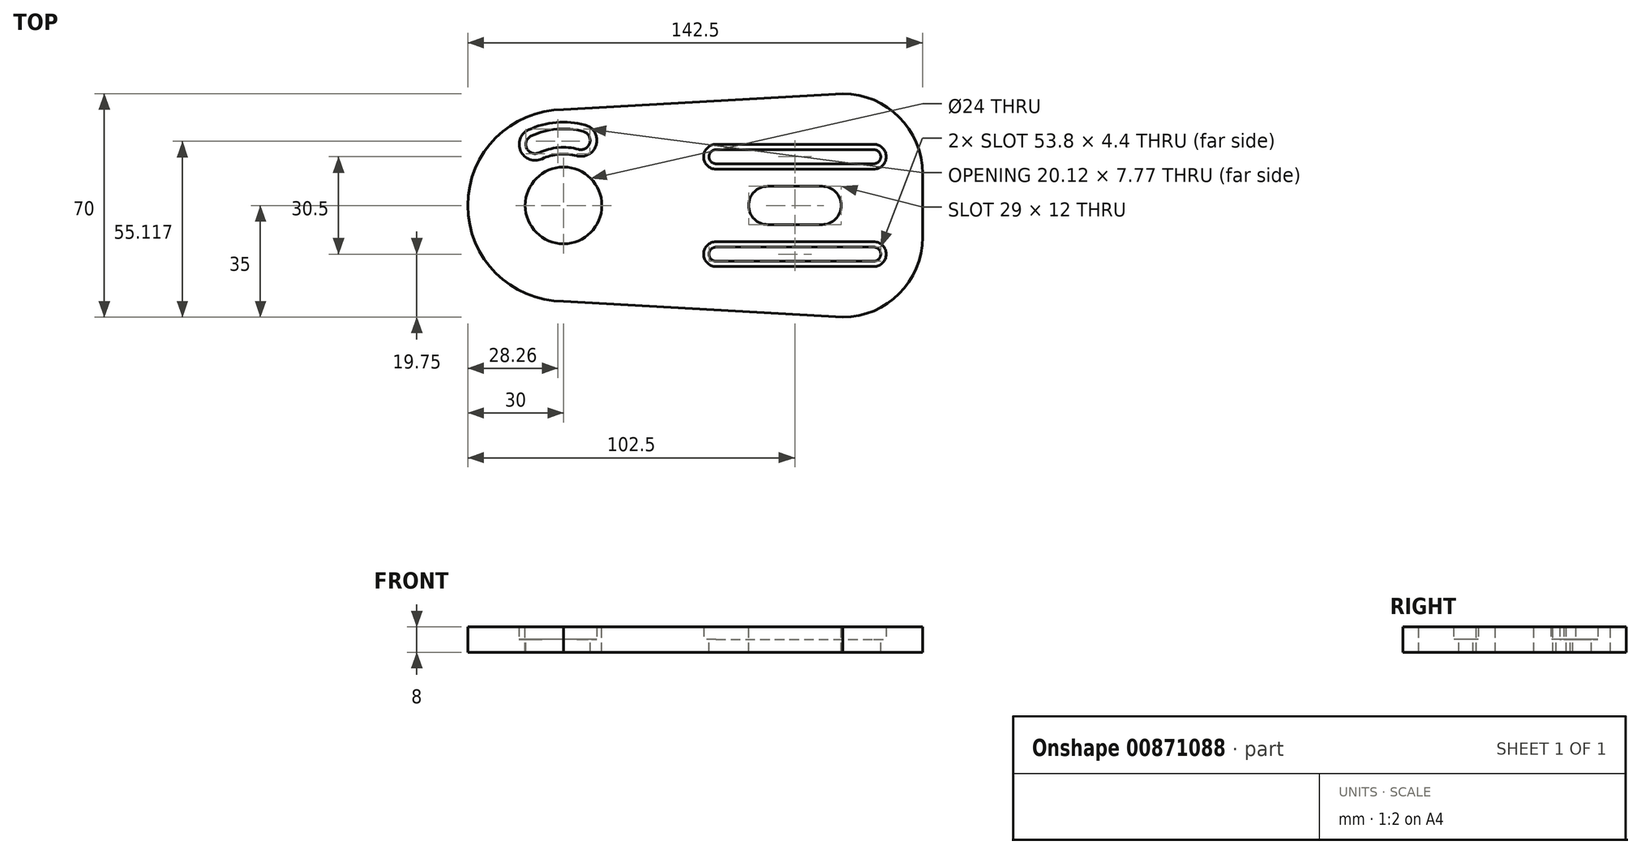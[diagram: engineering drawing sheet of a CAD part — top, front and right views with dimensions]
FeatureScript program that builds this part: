
annotation { "Feature Type Name" : "Feature", "Feature Type Description" : "" }
export const myFeature = defineFeature(function(context is Context, id is Id, definition is map)
    precondition{}
    {
        {
            var Q0;
            Q0=qCreatedBy(makeId("Top.planeOp"),FACE);
            var sketch = newSketch(context, id + "F0", { "sketchPlane" : qUnion([Q0])});
            skLineSegment(sketch, "E0.bottom", {"start": v(39.15, 35) * mm, "end": v(-48.35, 35) * mm, "construction": true});
            skLineSegment(sketch, "E0.top", {"start": v(39.15, -35) * mm, "end": v(-48.35, -35) * mm, "construction": true});
            skLineSegment(sketch, "E0.left", {"start": v(64.15, 10) * mm, "end": v(64.15, -10) * mm});
            skPoint(sketch, "E0.middle", {"position": v(0, 0) * mm});
            skCircle(sketch, "E1", {"center": v(-48.35, 0) * mm, "radius": 12 * mm});
            skArc(sketch, "E2.filletArc", {"start": v(64.15, 10) * mm, "mid": v(56.83, 27.68) * mm, "end": v(39.15, 35) * mm});
            skArc(sketch, "E3.filletArc", {"start": v(39.15, -35) * mm, "mid": v(56.83, -27.68) * mm, "end": v(64.15, -10) * mm});
            skLineSegment(sketch, "E4.bottom", {"start": v(32.65, 6) * mm, "end": v(24.15, 6) * mm});
            skPoint(sketch, "E4.middle", {"position": v(24.15, 0) * mm});
            skLineSegment(sketch, "E5", {"start": v(-48.35, 0) * mm, "end": v(-49.94, 18.13) * mm, "construction": true});
            skPoint(sketch, "E6", {"position": v(64.15, 0) * mm});
            skArc(sketch, "E7", {"start": v(-59.36, 23.66) * mm, "mid": v(-61.78, 17.02) * mm, "end": v(-55.14, 14.6) * mm});
            skArc(sketch, "E8", {"start": v(-58.47, 21.76) * mm, "mid": v(-59.88, 17.9) * mm, "end": v(-56.03, 16.5) * mm});
            skArc(sketch, "E9", {"start": v(-43.65, 17.58) * mm, "mid": v(-40.1, 19.64) * mm, "end": v(-42.16, 23.19) * mm});
            skArc(sketch, "E10.trimOffspring", {"start": v(-44.2, 15.55) * mm, "mid": v(-49.75, 16.04) * mm, "end": v(-55.14, 14.6) * mm});
            skArc(sketch, "E11.trimOffspring", {"start": v(-43.65, 17.58) * mm, "mid": v(-49.94, 18.13) * mm, "end": v(-56.03, 16.5) * mm});
            skArc(sketch, "E12.trimOffspring", {"start": v(-42.16, 23.19) * mm, "mid": v(-50.44, 23.9) * mm, "end": v(-58.47, 21.76) * mm});
            skArc(sketch, "E13.trimOffspring", {"start": v(-41.62, 25.22) * mm, "mid": v(-50.62, 26) * mm, "end": v(-59.36, 23.66) * mm});
            skArc(sketch, "E14.trimOffspring", {"start": v(-44.2, 15.55) * mm, "mid": v(-38.08, 19.1) * mm, "end": v(-41.62, 25.22) * mm});
            skCircle(sketch, "E15", {"center": v(-48.35, 0) * mm, "radius": 21.1 * mm, "construction": true});
            skLineSegment(sketch, "E16", {"start": v(32.65, 0) * mm, "end": v(24.15, 0) * mm, "construction": true});
            skArc(sketch, "E17", {"start": v(32.65, -6) * mm, "mid": v(38.65, 0) * mm, "end": v(32.65, 6) * mm});
            skLineSegment(sketch, "E18", {"start": v(24.15, 0) * mm, "end": v(24.15, 6) * mm, "construction": true});
            skLineSegment(sketch, "E19.MirrorCS", {"start": v(32.65, -6) * mm, "end": v(24.15, -6) * mm});
            skLineSegment(sketch, "E20.MirrorCS", {"start": v(15.65, 6) * mm, "end": v(24.15, 6) * mm});
            skArc(sketch, "E21.MirrorCS", {"start": v(15.65, -6) * mm, "mid": v(9.65, 0) * mm, "end": v(15.65, 6) * mm});
            skLineSegment(sketch, "E22.MirrorCS", {"start": v(15.65, -6) * mm, "end": v(24.15, -6) * mm});
            skArc(sketch, "E23", {"start": v(-0.55, -11.35) * mm, "mid": v(-4.45, -15.25) * mm, "end": v(-0.55, -19.15) * mm});
            skArc(sketch, "E24", {"start": v(-0.55, -13.05) * mm, "mid": v(-2.75, -15.25) * mm, "end": v(-0.55, -17.45) * mm});
            skLineSegment(sketch, "E25", {"start": v(-0.55, -11.35) * mm, "end": v(24.15, -11.35) * mm});
            skLineSegment(sketch, "E26", {"start": v(-0.55, -15.25) * mm, "end": v(24.15, -15.25) * mm, "construction": true});
            skLineSegment(sketch, "E27", {"start": v(-0.55, -13.05) * mm, "end": v(24.15, -13.05) * mm});
            skLineSegment(sketch, "E28.MirrorCS", {"start": v(-0.55, -17.45) * mm, "end": v(24.15, -17.45) * mm});
            skLineSegment(sketch, "E29.MirrorCS", {"start": v(-0.55, -19.15) * mm, "end": v(24.15, -19.15) * mm});
            skLineSegment(sketch, "E30.MirrorCS", {"start": v(48.85, -11.35) * mm, "end": v(24.15, -11.35) * mm});
            skLineSegment(sketch, "E31.MirrorCS", {"start": v(48.85, -13.05) * mm, "end": v(24.15, -13.05) * mm});
            skLineSegment(sketch, "E32.MirrorCS", {"start": v(48.85, -17.45) * mm, "end": v(24.15, -17.45) * mm});
            skLineSegment(sketch, "E33.MirrorCS", {"start": v(48.85, -19.15) * mm, "end": v(24.15, -19.15) * mm});
            skArc(sketch, "E34.MirrorCS", {"start": v(48.85, -13.05) * mm, "mid": v(51.05, -15.25) * mm, "end": v(48.85, -17.45) * mm});
            skArc(sketch, "E35.MirrorCS", {"start": v(48.85, -11.35) * mm, "mid": v(52.75, -15.25) * mm, "end": v(48.85, -19.15) * mm});
            skLineSegment(sketch, "E36.MirrorCS", {"start": v(-0.55, 11.35) * mm, "end": v(24.15, 11.35) * mm});
            skArc(sketch, "E37.MirrorCS", {"start": v(-0.55, 11.35) * mm, "mid": v(-4.45, 15.25) * mm, "end": v(-0.55, 19.15) * mm});
            skArc(sketch, "E38.MirrorCS", {"start": v(-0.55, 13.05) * mm, "mid": v(-2.75, 15.25) * mm, "end": v(-0.55, 17.45) * mm});
            skLineSegment(sketch, "E39.MirrorCS", {"start": v(-0.55, 13.05) * mm, "end": v(24.15, 13.05) * mm});
            skLineSegment(sketch, "E40.MirrorCS", {"start": v(-0.55, 17.45) * mm, "end": v(24.15, 17.45) * mm});
            skLineSegment(sketch, "E41.MirrorCS", {"start": v(-0.55, 19.15) * mm, "end": v(24.15, 19.15) * mm});
            skLineSegment(sketch, "E42.MirrorCS", {"start": v(48.85, 19.15) * mm, "end": v(24.15, 19.15) * mm});
            skLineSegment(sketch, "E43.MirrorCS", {"start": v(48.85, 17.45) * mm, "end": v(24.15, 17.45) * mm});
            skLineSegment(sketch, "E44.MirrorCS", {"start": v(48.85, 13.05) * mm, "end": v(24.15, 13.05) * mm});
            skLineSegment(sketch, "E45.MirrorCS", {"start": v(48.85, 11.35) * mm, "end": v(24.15, 11.35) * mm});
            skArc(sketch, "E46.MirrorCS", {"start": v(48.85, 11.35) * mm, "mid": v(52.75, 15.25) * mm, "end": v(48.85, 19.15) * mm});
            skArc(sketch, "E47.MirrorCS", {"start": v(48.85, 13.05) * mm, "mid": v(51.05, 15.25) * mm, "end": v(48.85, 17.45) * mm});
            skLineSegment(sketch, "E48.anchor1", {"start": v(-48.35, 0) * mm, "end": v(-44.2, 15.55) * mm, "construction": true});
            skCircle(sketch, "E49", {"center": v(24.15, 0) * mm, "radius": 31.5 * mm, "construction": true});
            skCircle(sketch, "E50", {"center": v(-48.35, 0) * mm, "radius": 28 * mm, "construction": true});
            skCircle(sketch, "E51", {"center": v(32.65, 0) * mm, "radius": 31.5 * mm, "construction": true});
            skCircle(sketch, "E52", {"center": v(15.65, 0) * mm, "radius": 31.5 * mm, "construction": true});
            skLineSegment(sketch, "E53", {"start": v(-48.35, 0) * mm, "end": v(-48.35, -30) * mm, "construction": true});
            skLineSegment(sketch, "E54.MirrorCS", {"start": v(-48.35, 0) * mm, "end": v(-48.35, 30) * mm, "construction": true});
            skLineSegment(sketch, "E55", {"start": v(39.15, 35) * mm, "end": v(-48.35, 30) * mm});
            skLineSegment(sketch, "E56", {"start": v(39.15, -35) * mm, "end": v(-48.35, -30) * mm});
            skArc(sketch, "E57", {"start": v(-48.35, 30) * mm, "mid": v(-78.35, 0) * mm, "end": v(-48.35, -30) * mm});
            skSolve(sketch);
        }
        {
            var Q0;
            Q0=qSketchRegion(id+"F0",true);
            var Q1;
            Q1=makeQuery(id+"F0.imprint","IMPRINT",FACE,{"disambiguationData":[TD([[makeQuery(id+"F0.imprint","IMPRINT",EDGE,{"derivedFrom":sQuery(id+"F0.wireOp",EDGE,"E7")}),1.0]])]});
            var Q2;
            Q2=makeQuery(id+"F0.imprint","IMPRINT",FACE,{"disambiguationData":[TD([[makeQuery(id+"F0.imprint","IMPRINT",EDGE,{"derivedFrom":sQuery(id+"F0.wireOp",EDGE,"s4kBiPaO-k1EP-gunY-A6fh-K6L33tH7EWGI")}),1.0]])]});
            var Q3;
            Q3=makeQuery(id+"F0.imprint","IMPRINT",FACE,{"disambiguationData":[TD([[makeQuery(id+"F0.imprint","IMPRINT",EDGE,{"derivedFrom":sQuery(id+"F0.wireOp",EDGE,"gth151Oa-FUtn-34ZQ-c7lR-fLvkNPwmrSFz")}),1.0]])]});
            var Q4;
            Q4=makeQuery(id+"F0.imprint","IMPRINT",FACE,{"disambiguationData":[TD([[makeQuery(id+"F0.imprint","IMPRINT",EDGE,{"derivedFrom":sQuery(id+"F0.wireOp",EDGE,"951b57d0-023d-4b59-83ac-9b7100598cb4.bottom")}),1.0]])]});
            var Q5;
            Q5=makeQuery(id+"F0.imprint","IMPRINT",FACE,{"disambiguationData":[TD([[makeQuery(id+"F0.imprint","IMPRINT",EDGE,{"derivedFrom":sQuery(id+"F0.wireOp",EDGE,"4f684b0e-bc20-43cd-95fc-20f0ed7439a4.bottom")}),1.0]])]});
            var Q6;
            Q6=makeQuery(id+"F0.imprint","IMPRINT",FACE,{"disambiguationData":[TD([[makeQuery(id+"F0.imprint","IMPRINT",EDGE,{"derivedFrom":sQuery(id+"F0.wireOp",EDGE,"E48.1.0")}),1.0]])]});
            var Q7;
            Q7=makeQuery(id+"F0.imprint","IMPRINT",FACE,{"disambiguationData":[TD([[makeQuery(id+"F0.imprint","IMPRINT",EDGE,{"derivedFrom":sQuery(id+"F0.wireOp",EDGE,"E48.2.0")}),1.0]])]});
            var Q8;
            Q8=makeQuery(id+"F0.imprint","IMPRINT",FACE,{"disambiguationData":[TD([[makeQuery(id+"F0.imprint","IMPRINT",EDGE,{"derivedFrom":sQuery(id+"F0.wireOp",EDGE,"E36.MirrorCS")}),1.0]])]});
            var Q9;
            Q9=makeQuery(id+"F0.imprint","IMPRINT",FACE,{"disambiguationData":[TD([[makeQuery(id+"F0.imprint","IMPRINT",EDGE,{"derivedFrom":sQuery(id+"F0.wireOp",EDGE,"E23")}),1.0]])]});
            extrude(context, id + "F1", {"entities" : qUnion([Q0, Q1, Q2, Q3, Q4, Q5, Q6, Q7, Q8, Q9]), "oppositeDirection" : true, "depth" : 4 * mm, "offsetDistance" : 25 * mm});
        }
        {
            var Q0;
            Q0=qSketchRegion(id+"F0",true);
            extrude(context, id + "F2", {"entities" : qUnion([Q0]), "operationType" : NewBodyOperationType.ADD, "depth" : 4 * mm, "offsetDistance" : 25 * mm});
        }
    });
